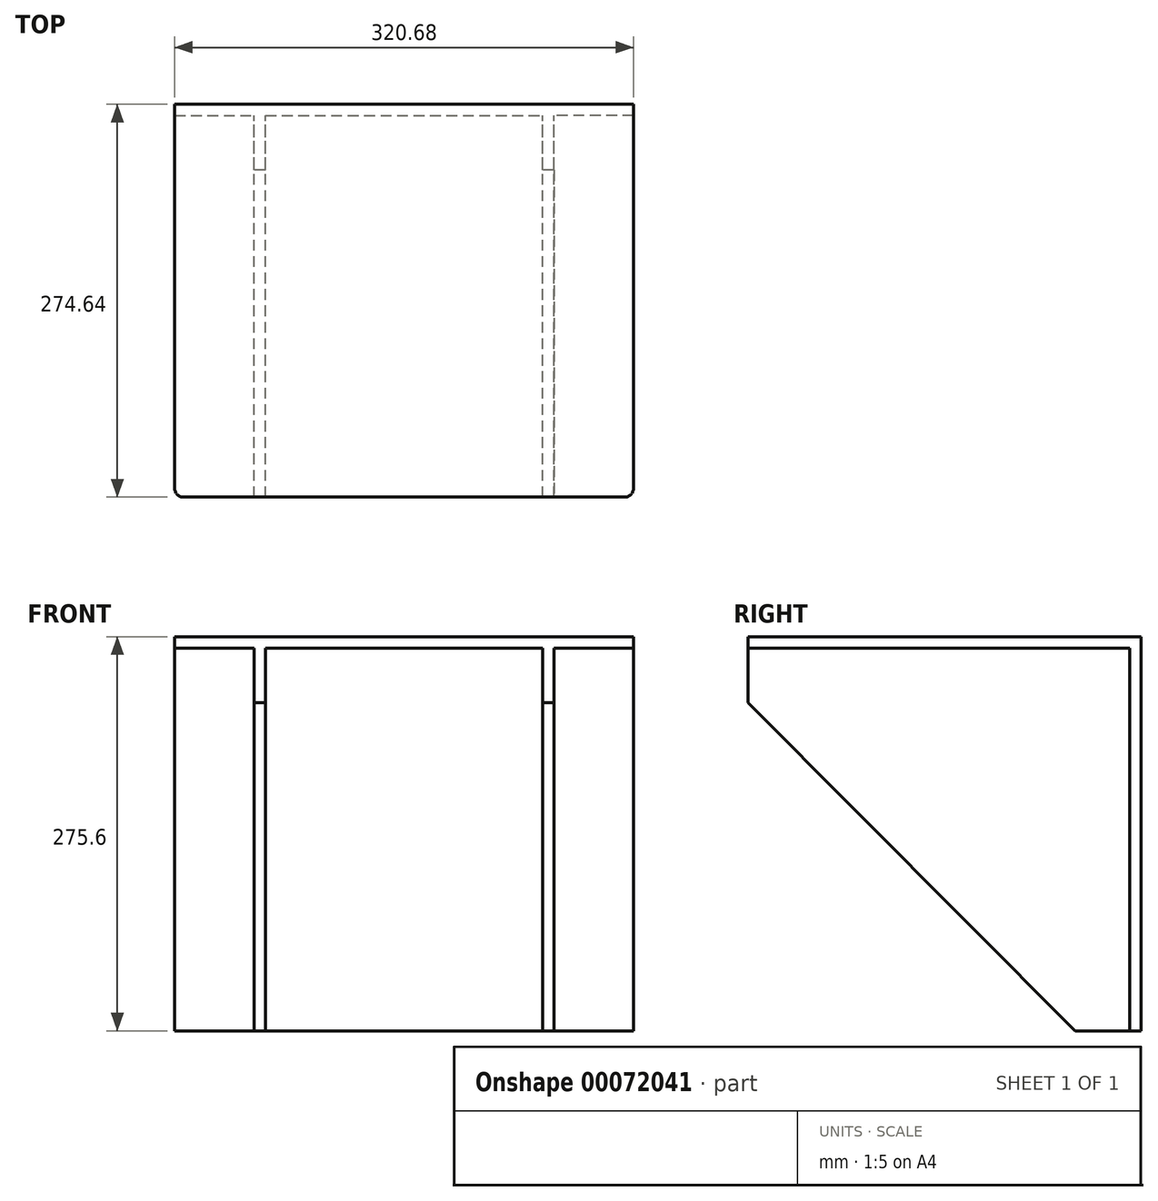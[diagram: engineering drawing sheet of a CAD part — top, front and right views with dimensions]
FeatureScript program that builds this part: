
annotation { "Feature Type Name" : "Feature", "Feature Type Description" : "" }
export const myFeature = defineFeature(function(context is Context, id is Id, definition is map)
    precondition{}
    {
        {
            var Q0;
            Q0=qCreatedBy(makeId("Front.planeOp"),FACE);
            var sketch = newSketch(context, id + "F0", { "sketchPlane" : qUnion([Q0])});
            skLineSegment(sketch, "E0.bottom", {"start": v(-160.34, 0) * mm, "end": v(160.34, 0) * mm});
            skLineSegment(sketch, "E0.top", {"start": v(-160.34, -275.6) * mm, "end": v(160.34, -275.6) * mm});
            skLineSegment(sketch, "E0.left", {"start": v(-160.34, 0) * mm, "end": v(-160.34, -275.6) * mm});
            skLineSegment(sketch, "E0.right", {"start": v(160.34, 0) * mm, "end": v(160.34, -275.6) * mm});
            skSolve(sketch);
        }
        {
            var Q0;
            Q0=makeQuery(id+"F0.imprint","IMPRINT",FACE,{"disambiguationData":[TD([[makeQuery(id+"F0.imprint","IMPRINT",EDGE,{"derivedFrom":sQuery(id+"F0.wireOp",EDGE,"E0.bottom")}),-1.0]])]});
            extrude(context, id + "F1", {"entities" : qUnion([Q0]), "depth" : 7.94 * mm});
        }
        {
            var Q0;
            Q0=makeQuery(id+"F1.opExtrude","CAP_FACE",FACE,{"disambiguationData":[OSD([sQuery(id+"F0.wireOp",EDGE,"E0.bottom"),sQuery(id+"F0.wireOp",EDGE,"E0.top"),sQuery(id+"F0.wireOp",EDGE,"E0.left"),sQuery(id+"F0.wireOp",EDGE,"E0.right")])],"isStart":false});
            var sketch = newSketch(context, id + "F2", { "sketchPlane" : qUnion([Q0])});
            skLineSegment(sketch, "E1.bottom", {"start": v(-128.59, -193.05) * mm, "end": v(128.59, -193.05) * mm});
            skLineSegment(sketch, "E1.top", {"start": v(-128.59, -256.55) * mm, "end": v(128.59, -256.55) * mm});
            skLineSegment(sketch, "E1.left", {"start": v(-128.59, -193.05) * mm, "end": v(-128.59, -256.55) * mm});
            skLineSegment(sketch, "E1.right", {"start": v(128.59, -193.05) * mm, "end": v(128.59, -256.55) * mm});
            skSolve(sketch);
        }
        {
            var Q0;
            Q0=makeQuery(id+"F1.opExtrude","CAP_FACE",FACE,{"disambiguationData":[OSD([sQuery(id+"F0.wireOp",EDGE,"E0.bottom"),sQuery(id+"F0.wireOp",EDGE,"E0.top"),sQuery(id+"F0.wireOp",EDGE,"E0.left"),sQuery(id+"F0.wireOp",EDGE,"E0.right")])],"isStart":false});
            var sketch = newSketch(context, id + "F3", { "sketchPlane" : qUnion([Q0])});
            skLineSegment(sketch, "E2", {"start": v(-160.34, 0) * mm, "end": v(-160.34, -7.94) * mm});
            skLineSegment(sketch, "E3", {"start": v(-160.34, -7.94) * mm, "end": v(-104.78, -7.94) * mm});
            skLineSegment(sketch, "E4", {"start": v(-104.78, -7.94) * mm, "end": v(-104.78, -275.6) * mm});
            skLineSegment(sketch, "E5", {"start": v(-104.78, -275.6) * mm, "end": v(-96.84, -275.6) * mm});
            skLineSegment(sketch, "E6", {"start": v(-96.84, -275.6) * mm, "end": v(-96.84, -7.94) * mm});
            skLineSegment(sketch, "E7.MirrorCS", {"start": v(160.34, -7.94) * mm, "end": v(104.78, -7.94) * mm});
            skLineSegment(sketch, "E8.MirrorCS", {"start": v(96.84, -275.6) * mm, "end": v(96.84, -7.94) * mm});
            skLineSegment(sketch, "E9.MirrorCS", {"start": v(104.78, -7.94) * mm, "end": v(104.78, -275.6) * mm});
            skLineSegment(sketch, "E10.MirrorCS", {"start": v(104.78, -275.6) * mm, "end": v(96.84, -275.6) * mm});
            skLineSegment(sketch, "E11.MirrorCS", {"start": v(160.34, 0) * mm, "end": v(160.34, -7.94) * mm});
            skLineSegment(sketch, "E12", {"start": v(-96.84, -7.94) * mm, "end": v(96.84, -7.94) * mm});
            skLineSegment(sketch, "E13", {"start": v(-160.34, 0) * mm, "end": v(160.34, 0) * mm});
            skSolve(sketch);
        }
        {
            var Q0;
            Q0 = qSketchRegion(id + "F3", true);
            extrude(context, id + "F4", {"entities" : qUnion([Q0]), "operationType" : NewBodyOperationType.ADD, "depth" : 266.7 * mm});
        }
        {
            var Q0;
            Q0=makeQuery(id+"F4.opExtrude","SWEPT_FACE",FACE,{"disambiguationData":[OSD([sQuery(id+"F3.wireOp",EDGE,"E4")])]});
            var sketch = newSketch(context, id + "F5", { "sketchPlane" : qUnion([Q0])});
            skLineSegment(sketch, "E14", {"start": v(46.04, -275.6) * mm, "end": v(274.64, -275.6) * mm});
            skLineSegment(sketch, "E15", {"start": v(274.64, -275.6) * mm, "end": v(274.64, -46.04) * mm});
            skLineSegment(sketch, "E16", {"start": v(274.64, -46.04) * mm, "end": v(46.04, -275.6) * mm});
            skSolve(sketch);
        }
        {
            var Q0;
            Q0 = qSketchRegion(id + "F5", true);
            extrude(context, id + "F6", {"entities" : qUnion([Q0]), "operationType" : NewBodyOperationType.REMOVE, "endBound" : BoundingType.THROUGH_ALL, "oppositeDirection" : true, "depth" : 25.4 * mm});
        }
        {
            var Q0;
            Q0=makeQuery(id+"F4.boolean.opBoolean","MERGE",FACE,{"derivedFrom":[makeQuery(id+"F1.opExtrude","SWEPT_FACE",FACE,{"disambiguationData":[OSD([sQuery(id+"F0.wireOp",EDGE,"E0.bottom")])]}),makeQuery(id+"F4.opExtrude","SWEPT_FACE",FACE,{"disambiguationData":[OSD([sQuery(id+"F3.wireOp",EDGE,"E13")])]})]});
            var sketch = newSketch(context, id + "F7", { "sketchPlane" : qUnion([Q0])});
            skLineSegment(sketch, "E17.bottom", {"start": v(-50, -139.85) * mm, "end": v(50, -139.85) * mm});
            skLineSegment(sketch, "E17.top", {"start": v(-50, -239.85) * mm, "end": v(50, -239.85) * mm});
            skLineSegment(sketch, "E17.left", {"start": v(-50, -139.85) * mm, "end": v(-50, -239.85) * mm});
            skLineSegment(sketch, "E17.right", {"start": v(50, -139.85) * mm, "end": v(50, -239.85) * mm});
            skSolve(sketch);
        }
        {
            var Q0;
            Q0=makeQuery(id+"F4.opExtrude","CAP_EDGE",EDGE,{"disambiguationData":[OSD([sQuery(id+"F3.wireOp",EDGE,"E2")])],"isStart":false});
            var Q1;
            Q1=makeQuery(id+"F4.opExtrude","CAP_EDGE",EDGE,{"disambiguationData":[OSD([sQuery(id+"F3.wireOp",EDGE,"E11.MirrorCS")])],"isStart":false});
            fillet(context, id + "F8", {"entities" : qUnion([Q0, Q1]), "radius" : 6.35 * mm, "tangentPropagation" : true, "allowEdgeOverflow" : false});
        }
    });
